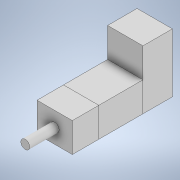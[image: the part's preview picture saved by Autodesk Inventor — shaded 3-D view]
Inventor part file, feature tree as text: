
AUTODESK INVENTOR PART (.ipt)
format: ipt  version: 2020 (Build 240168000, 168)  size: 125,952 bytes
history: native  units: mm
features: extrude x4, sketch x4, projected_geometry x1
ambient origin geometry x8: Origin, YZ Plane, XZ Plane, XY Plane, X Axis, Y Axis, Z Axis, Center Point
bodies: Solid1 (feature_tree), Solid2 (feature_tree), Solid3 (feature_tree)
feature tree (9):
  extrude  "Extrusion1"  Depth=10.0mm
  extrude  "Extrusion2"  Depth=15.0mm TaperAngle=0.0deg
  extrude  "Extrusion3"  Depth=10.0mm TaperAngle=0.0deg
  extrude  "Extrusion4"  Depth=10.0mm TaperAngle=0.0deg
  sketch  "Sketch1"  dims[d0=12.0mm d1=10.0mm]
  sketch  "Sketch2"  dims[d2=9.0mm d3=0.0mm d4=15.0mm d5=0.0mm]
  projected_geometry  "Projected Loop1"
  sketch  "Sketch3"  dims[d6=10.0mm d7=10.0mm d8=0.0mm]
  sketch  "Sketch4"  dims[d9=3.0mm d10=10.0mm d11=0.0mm]
